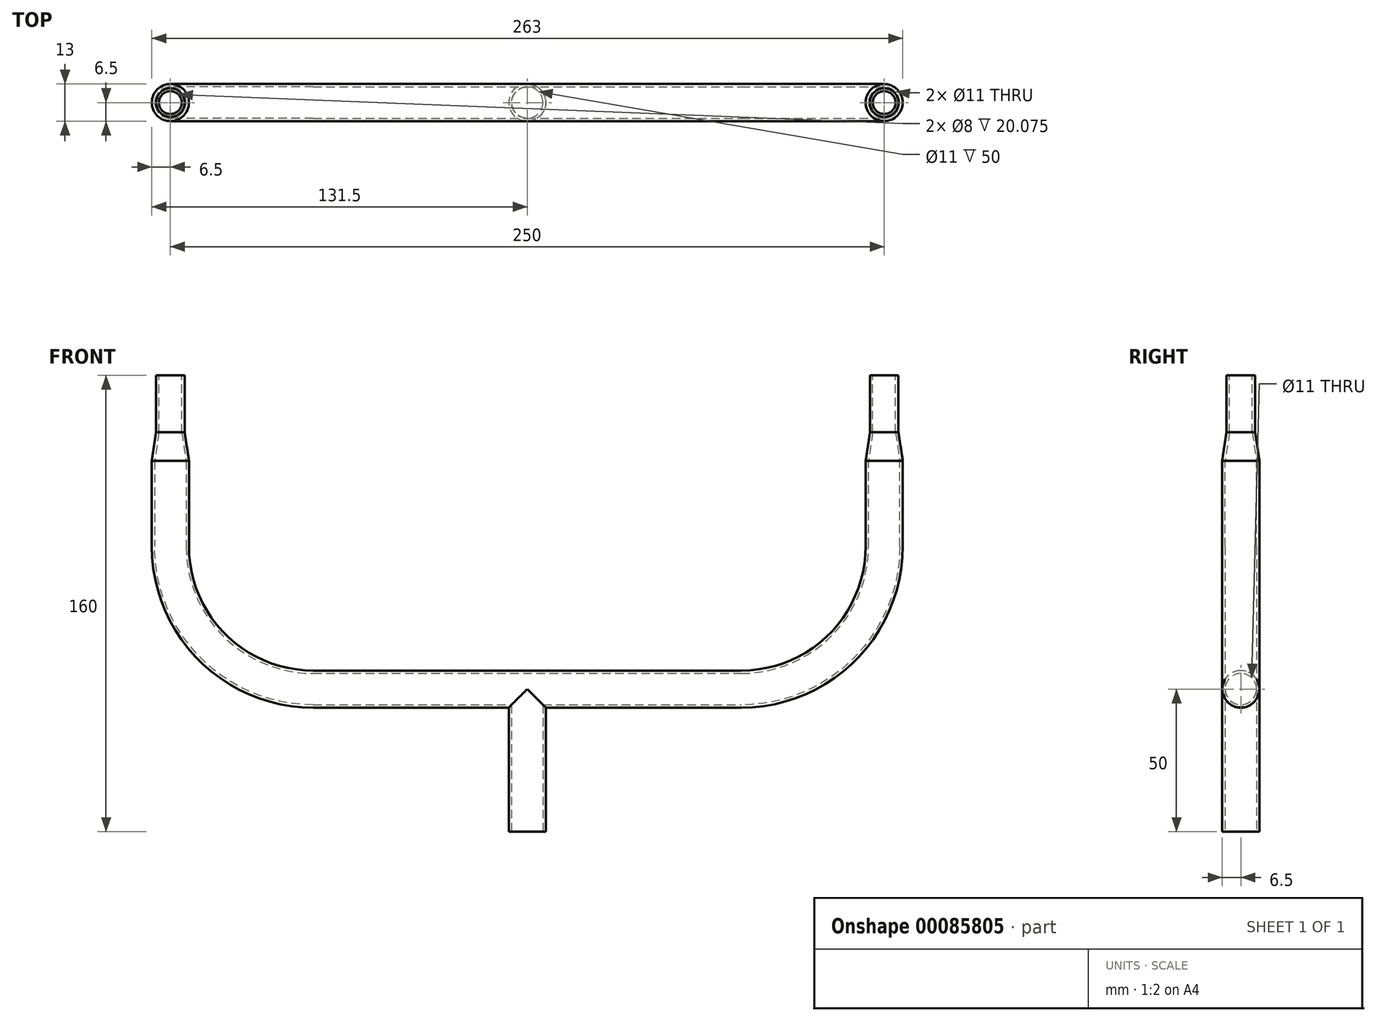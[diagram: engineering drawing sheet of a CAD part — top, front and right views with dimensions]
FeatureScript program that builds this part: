
annotation { "Feature Type Name" : "Feature", "Feature Type Description" : "" }
export const myFeature = defineFeature(function(context is Context, id is Id, definition is map)
    precondition{}
    {
        {
            var Q0;
            Q0=qCreatedBy(makeId("Front.planeOp"),FACE);
            var sketch = newSketch(context, id + "F0", { "sketchPlane" : qUnion([Q0])});
            skLineSegment(sketch, "E0", {"start": v(-75, 50) * mm, "end": v(75, 50) * mm});
            skArc(sketch, "E1", {"start": v(-75, 50) * mm, "mid": v(-110.36, 64.64) * mm, "end": v(-125, 100) * mm});
            skArc(sketch, "E2", {"start": v(75, 50) * mm, "mid": v(110.36, 64.64) * mm, "end": v(125, 100) * mm});
            skLineSegment(sketch, "E3", {"start": v(-125, 100) * mm, "end": v(-125, 120) * mm});
            skLineSegment(sketch, "E4", {"start": v(125, 100) * mm, "end": v(125, 120) * mm});
            skSolve(sketch);
        }
        {
            var Q0;
            Q0=qCreatedBy(makeId("Top.planeOp"),FACE);
            var Q1;
            Q1=sQuery(id+"F0.wireOp",VERTEX,"E3.end");
            cPlane(context, id + "F1", {"entities" : qUnion([Q0, Q1]), "cplaneType" : CPlaneType.PLANE_POINT, "offset" : 100 * mm, "width" : 150 * mm, "height" : 150 * mm});
        }
        {
            var Q0;
            Q0=qCreatedBy(id+"F1.planeOp",FACE);
            var sketch = newSketch(context, id + "F2", { "sketchPlane" : qUnion([Q0])});
            skCircle(sketch, "E5", {"center": v(-125, 0) * mm, "radius": 6.5 * mm});
            skCircle(sketch, "E6.0", {"center": v(-125, 0) * mm, "radius": 5.5 * mm});
            skSolve(sketch);
        }
        {
            var Q0;
            Q0=makeQuery(id+"F2.imprint","IMPRINT",FACE,{"disambiguationData":[TD([[makeQuery(id+"F2.imprint","IMPRINT",EDGE,{"derivedFrom":sQuery(id+"F2.wireOp",EDGE,"E5")}),1.0]])]});
            var Q1;
            Q1 = qConstructionFilter(qBodyType(qCreatedBy(id + "F0" ,EDGE), BodyType.WIRE), ConstructionObject.NO);
            sweep(context, id + "F3", {"profiles" : qUnion([Q0]), "path" : qUnion([Q1])});
        }
        {
            var Q0;
            Q0=qCreatedBy(makeId("Top.planeOp"),FACE);
            var sketch = newSketch(context, id + "F4", { "sketchPlane" : qUnion([Q0])});
            skCircle(sketch, "E7", {"center": v(0, 0) * mm, "radius": 5.5 * mm});
            skSolve(sketch);
        }
        {
            var Q0;
            Q0 = qSketchRegion(id + "F4", true);
            extrude(context, id + "F5", {"entities" : qUnion([Q0]), "operationType" : NewBodyOperationType.REMOVE, "depth" : 50 * mm});
        }
        {
            var Q0;
            Q0=qCreatedBy(makeId("Top.planeOp"),FACE);
            var sketch = newSketch(context, id + "F6", { "sketchPlane" : qUnion([Q0])});
            skCircle(sketch, "E8", {"center": v(0, 0) * mm, "radius": 6.5 * mm});
            skCircle(sketch, "E9", {"center": v(0, 0) * mm, "radius": 5.5 * mm});
            skSolve(sketch);
        }
        {
            var Q0;
            Q0=makeQuery(id+"F6.imprint","IMPRINT",FACE,{"disambiguationData":[TD([[makeQuery(id+"F6.imprint","IMPRINT",EDGE,{"derivedFrom":sQuery(id+"F6.wireOp",EDGE,"E8")}),1.0]])]});
            extrude(context, id + "F7", {"entities" : qUnion([Q0]), "operationType" : NewBodyOperationType.ADD, "endBound" : BoundingType.UP_TO_NEXT, "depth" : 25 * mm});
        }
        {
            var Q0;
            Q0=qCreatedBy(makeId("Front.planeOp"),FACE);
            var sketch = newSketch(context, id + "F8", { "sketchPlane" : qUnion([Q0])});
            skLineSegment(sketch, "E10", {"start": v(-125, 160) * mm, "end": v(-125, 120) * mm, "construction": true});
            skLineSegment(sketch, "E11", {"start": v(-118.5, 120) * mm, "end": v(-118.5, 130) * mm});
            skLineSegment(sketch, "E12", {"start": v(-118.5, 130) * mm, "end": v(-120, 140) * mm});
            skLineSegment(sketch, "E13", {"start": v(-120, 140) * mm, "end": v(-120, 160) * mm});
            skLineSegment(sketch, "E14.0", {"start": v(-121, 139.93) * mm, "end": v(-121, 160) * mm});
            skLineSegment(sketch, "E14.1", {"start": v(-119.5, 129.93) * mm, "end": v(-121, 139.93) * mm});
            skLineSegment(sketch, "E14.2", {"start": v(-119.5, 120) * mm, "end": v(-119.5, 129.93) * mm});
            skLineSegment(sketch, "E15", {"start": v(-118.5, 120) * mm, "end": v(-119.5, 120) * mm});
            skLineSegment(sketch, "E16", {"start": v(-121, 160) * mm, "end": v(-120, 160) * mm});
            skSolve(sketch);
        }
        {
            var Q0;
            Q0=makeQuery(id+"F8.imprint","IMPRINT",FACE,{"disambiguationData":[TD([[makeQuery(id+"F8.imprint","IMPRINT",EDGE,{"derivedFrom":sQuery(id+"F8.wireOp",EDGE,"E11")}),1.0]])]});
            var Q1;
            Q1=sQuery(id+"F8.wireOp",EDGE,"E10");
            revolve(context, id + "F9", {"operationType" : NewBodyOperationType.ADD, "entities" : qUnion([Q0]), "axis" : qUnion([Q1]), "revolveType" : RevolveType.FULL});
        }
        {
            var Q0;
            Q0=qCreatedBy(makeId("Front.planeOp"),FACE);
            var sketch = newSketch(context, id + "F10", { "sketchPlane" : qUnion([Q0])});
            skLineSegment(sketch, "E17", {"start": v(125, 160) * mm, "end": v(125, 120) * mm, "construction": true});
            skLineSegment(sketch, "E18", {"start": v(131.5, 120) * mm, "end": v(131.5, 130) * mm});
            skLineSegment(sketch, "E19", {"start": v(131.5, 130) * mm, "end": v(130, 140) * mm});
            skLineSegment(sketch, "E20", {"start": v(130, 140) * mm, "end": v(130, 160) * mm});
            skLineSegment(sketch, "E21.0", {"start": v(129, 139.93) * mm, "end": v(129, 160) * mm});
            skLineSegment(sketch, "E21.1", {"start": v(130.5, 129.93) * mm, "end": v(129, 139.93) * mm});
            skLineSegment(sketch, "E21.2", {"start": v(130.5, 120) * mm, "end": v(130.5, 129.93) * mm});
            skLineSegment(sketch, "E22", {"start": v(131.5, 120) * mm, "end": v(130.5, 120) * mm});
            skLineSegment(sketch, "E23", {"start": v(129, 160) * mm, "end": v(130, 160) * mm});
            skSolve(sketch);
        }
        {
            var Q0;
            Q0=makeQuery(id+"F10.imprint","IMPRINT",FACE,{"disambiguationData":[TD([[makeQuery(id+"F10.imprint","IMPRINT",EDGE,{"derivedFrom":sQuery(id+"F10.wireOp",EDGE,"E18")}),1.0]])]});
            var Q1;
            Q1=sQuery(id+"F10.wireOp",EDGE,"E17");
            revolve(context, id + "F11", {"operationType" : NewBodyOperationType.ADD, "entities" : qUnion([Q0]), "axis" : qUnion([Q1]), "revolveType" : RevolveType.FULL});
        }
    });
